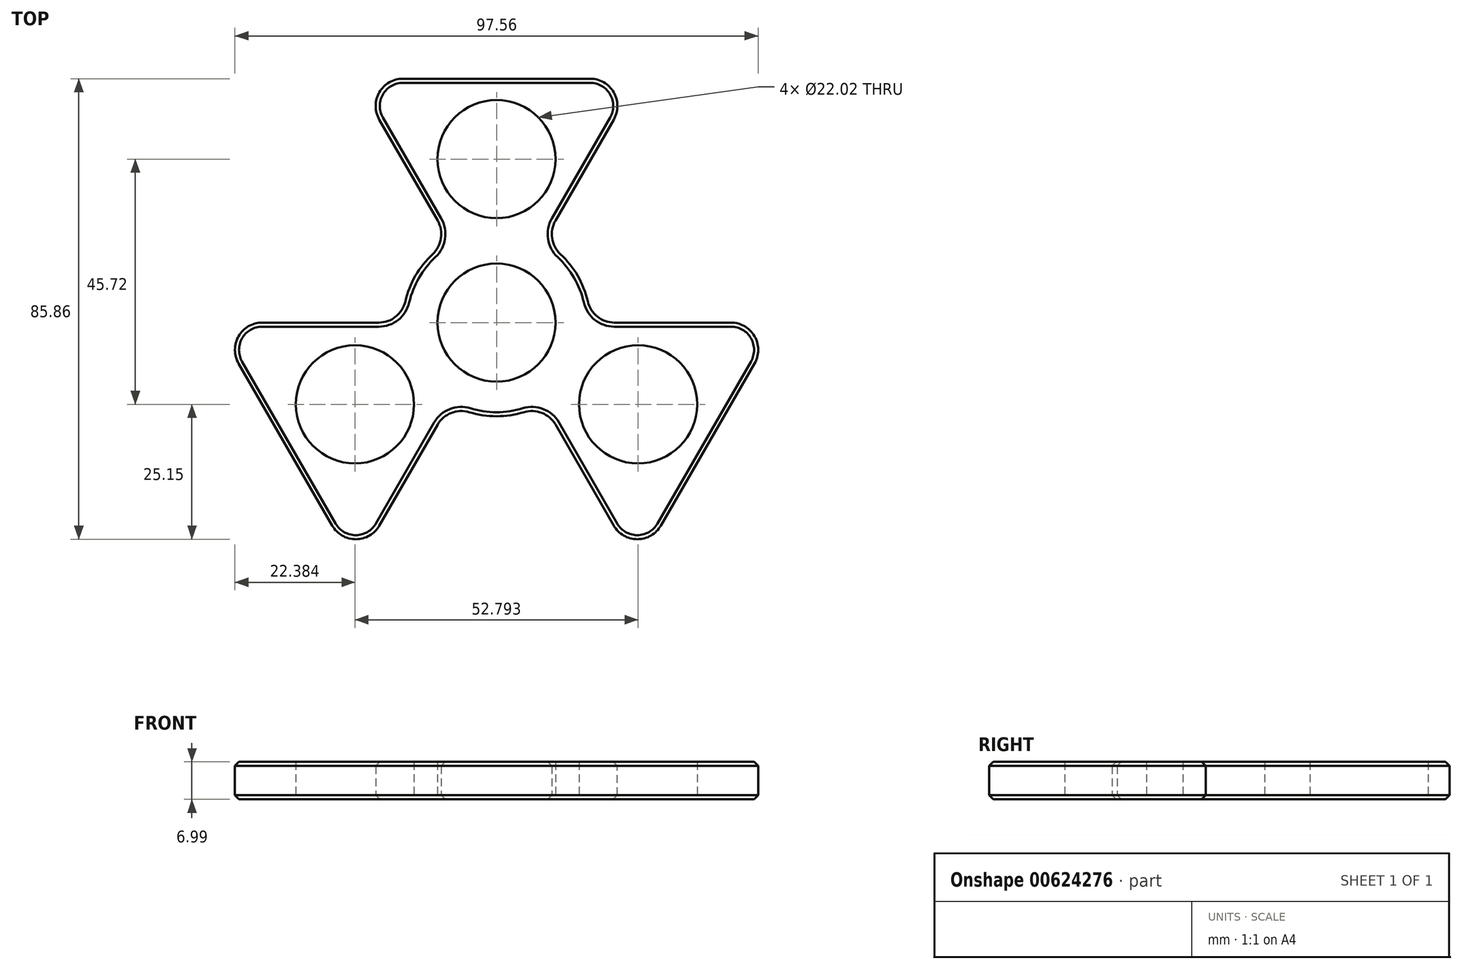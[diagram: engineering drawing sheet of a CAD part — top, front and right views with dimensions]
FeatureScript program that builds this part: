
annotation { "Feature Type Name" : "Feature", "Feature Type Description" : "" }
export const myFeature = defineFeature(function(context is Context, id is Id, definition is map)
    precondition{}
    {
        {
            var Q0;
            Q0=qCreatedBy(makeId("Top.planeOp"),FACE);
            var sketch = newSketch(context, id + "F0", { "sketchPlane" : qUnion([Q0])});
            skCircle(sketch, "E0", {"center": v(0, 0) * mm, "radius": 11.01 * mm});
            skLineSegment(sketch, "E1", {"start": v(0, 0) * mm, "end": v(-26.4, -15.24) * mm});
            skLineSegment(sketch, "E2", {"start": v(-26.4, -15.24) * mm, "end": v(0, 0) * mm});
            skLineSegment(sketch, "E3", {"start": v(0, 0) * mm, "end": v(26.4, -15.24) * mm});
            skLineSegment(sketch, "E4", {"start": v(26.4, -15.24) * mm, "end": v(0, 0) * mm});
            skLineSegment(sketch, "E5", {"start": v(0, 0) * mm, "end": v(0, 30.48) * mm});
            skCircle(sketch, "E6", {"center": v(-26.4, -15.24) * mm, "radius": 11.01 * mm});
            skCircle(sketch, "E7", {"center": v(26.4, -15.24) * mm, "radius": 11.01 * mm});
            skCircle(sketch, "E8", {"center": v(0, 30.48) * mm, "radius": 11.01 * mm});
            skCircle(sketch, "E9", {"center": v(0, 0) * mm, "radius": 14.82 * mm});
            skLineSegment(sketch, "E10", {"start": v(0, 30.48) * mm, "end": v(0, 45.47) * mm});
            skLineSegment(sketch, "E11", {"start": v(-26.4, -15.24) * mm, "end": v(-39.37, -22.73) * mm});
            skLineSegment(sketch, "E12", {"start": v(26.4, -15.24) * mm, "end": v(39.37, -22.73) * mm});
            skLineSegment(sketch, "E13", {"start": v(-39.37, -22.73) * mm, "end": v(-52.5, 0) * mm});
            skLineSegment(sketch, "E14", {"start": v(-39.37, -22.73) * mm, "end": v(-26.25, -45.47) * mm});
            skLineSegment(sketch, "E15", {"start": v(39.37, -22.73) * mm, "end": v(52.5, 0) * mm});
            skLineSegment(sketch, "E16", {"start": v(39.37, -22.73) * mm, "end": v(26.25, -45.47) * mm});
            skLineSegment(sketch, "E17", {"start": v(0, 45.47) * mm, "end": v(-26.25, 45.47) * mm});
            skLineSegment(sketch, "E18", {"start": v(0, 45.47) * mm, "end": v(26.25, 45.47) * mm});
            skLineSegment(sketch, "E19", {"start": v(-14.82, 0) * mm, "end": v(-52.5, 0) * mm});
            skLineSegment(sketch, "E20", {"start": v(-26.25, -45.47) * mm, "end": v(-7.41, -12.84) * mm});
            skLineSegment(sketch, "E21", {"start": v(26.25, -45.47) * mm, "end": v(7.41, -12.84) * mm});
            skLineSegment(sketch, "E22", {"start": v(14.82, 0) * mm, "end": v(52.5, 0) * mm});
            skLineSegment(sketch, "E23", {"start": v(-26.25, 45.47) * mm, "end": v(-7.41, 12.84) * mm});
            skLineSegment(sketch, "E24", {"start": v(26.25, 45.47) * mm, "end": v(7.41, 12.84) * mm});
            skCircle(sketch, "E25", {"center": v(0, 0) * mm, "radius": 17.46 * mm});
            skSolve(sketch);
        }
        {
            var Q0;
            Q0 = qSketchRegion(id + "F0", true);
            var Q1;
            {var subQ4=sQuery(id+"F0.wireOp",EDGE,"E0");var subQ6=sQuery(id+"F0.wireOp",EDGE,"E2");var subQ7=makeQuery(id+"F0.imprint","INTERSECT",VERTEX,{"derivedFrom":[subQ4,subQ6]});Q1=makeQuery(id+"F0.imprint","IMPRINT",FACE,{"disambiguationData":[TD([[makeQuery(id+"F0.imprint","IMPRINT",EDGE,{"disambiguationData":[TD([[subQ7,1.0]])],"derivedFrom":subQ4}),-1.0]])]});}
            var Q2;
            {var subQ4=sQuery(id+"F0.wireOp",EDGE,"E0");var subQ7=sQuery(id+"F0.wireOp",EDGE,"E5");var subQ8=makeQuery(id+"F0.imprint","INTERSECT",VERTEX,{"derivedFrom":[subQ4,subQ7]});Q2=makeQuery(id+"F0.imprint","IMPRINT",FACE,{"disambiguationData":[TD([[makeQuery(id+"F0.imprint","IMPRINT",EDGE,{"disambiguationData":[TD([[subQ8,1.0]])],"derivedFrom":subQ4}),-1.0]])]});}
            var Q3;
            {var subQ1=sQuery(id+"F0.wireOp",EDGE,"E0");var subQ5=sQuery(id+"F0.wireOp",EDGE,"E2");var subQ6=makeQuery(id+"F0.imprint","INTERSECT",VERTEX,{"derivedFrom":[subQ1,subQ5]});Q3=makeQuery(id+"F0.imprint","IMPRINT",FACE,{"disambiguationData":[TD([[makeQuery(id+"F0.imprint","IMPRINT",EDGE,{"disambiguationData":[TD([[subQ6,-1.0]])],"derivedFrom":subQ1}),-1.0]])]});}
            extrude(context, id + "F1", {"entities" : qUnion([Q0, Q1, Q2, Q3]), "depth" : 7 * mm, "offsetDistance" : 25.4 * mm});
        }
        {
            var Q0;
            Q0=makeQuery(id+"F1.opExtrude","SWEPT_EDGE",EDGE,{"disambiguationData":[OSD([sQuery(id+"F0.wireOp",EDGE,"E19"),sQuery(id+"F0.wireOp",EDGE,"jYicORtb-tOr6-X2Lc-VIRF-J2aUJWwLRQqY")])]});
            var Q1;
            Q1=makeQuery(id+"F1.opExtrude","SWEPT_EDGE",EDGE,{"disambiguationData":[OSD([sQuery(id+"F0.wireOp",EDGE,"E23"),sQuery(id+"F0.wireOp",EDGE,"jYicORtb-tOr6-X2Lc-VIRF-J2aUJWwLRQqY")])]});
            var Q2;
            Q2=makeQuery(id+"F1.opExtrude","SWEPT_EDGE",EDGE,{"disambiguationData":[OSD([sQuery(id+"F0.wireOp",EDGE,"E24"),sQuery(id+"F0.wireOp",EDGE,"jYicORtb-tOr6-X2Lc-VIRF-J2aUJWwLRQqY")])]});
            var Q3;
            Q3=makeQuery(id+"F1.opExtrude","SWEPT_EDGE",EDGE,{"disambiguationData":[OSD([sQuery(id+"F0.wireOp",EDGE,"E22"),sQuery(id+"F0.wireOp",EDGE,"jYicORtb-tOr6-X2Lc-VIRF-J2aUJWwLRQqY")])]});
            var Q4;
            Q4=makeQuery(id+"F1.opExtrude","SWEPT_EDGE",EDGE,{"disambiguationData":[OSD([sQuery(id+"F0.wireOp",EDGE,"E20"),sQuery(id+"F0.wireOp",EDGE,"jYicORtb-tOr6-X2Lc-VIRF-J2aUJWwLRQqY")])]});
            var Q5;
            Q5=makeQuery(id+"F1.opExtrude","SWEPT_EDGE",EDGE,{"disambiguationData":[OSD([sQuery(id+"F0.wireOp",EDGE,"E21"),sQuery(id+"F0.wireOp",EDGE,"jYicORtb-tOr6-X2Lc-VIRF-J2aUJWwLRQqY")])]});
            fillet(context, id + "F2", {"entities" : qUnion([Q0, Q1, Q2, Q3, Q4, Q5]), "radius" : 5.08 * mm, "tangentPropagation" : true, "allowEdgeOverflow" : false});
        }
        {
            var Q0;
            Q0=makeQuery(id+"F1.opExtrude","CAP_EDGE",EDGE,{"disambiguationData":[OSD([sQuery(id+"F0.wireOp",EDGE,"E19")])],"isStart":false});
            var Q1;
            Q1=makeQuery(id+"F1.opExtrude","CAP_EDGE",EDGE,{"disambiguationData":[OSD([sQuery(id+"F0.wireOp",EDGE,"E23")])],"isStart":false});
            var Q2;
            Q2=makeQuery(id+"F1.opExtrude","CAP_EDGE",EDGE,{"disambiguationData":[OSD([sQuery(id+"F0.wireOp",EDGE,"E22")])],"isStart":false});
            var Q3;
            Q3=makeQuery(id+"F1.opExtrude","CAP_EDGE",EDGE,{"disambiguationData":[OSD([sQuery(id+"F0.wireOp",EDGE,"E24")])],"isStart":false});
            var Q4;
            Q4=makeQuery(id+"F1.opExtrude","CAP_EDGE",EDGE,{"disambiguationData":[OSD([sQuery(id+"F0.wireOp",EDGE,"E17"),sQuery(id+"F0.wireOp",EDGE,"E18")])],"isStart":false});
            var Q5;
            Q5=makeQuery(id+"F1.opExtrude","CAP_EDGE",EDGE,{"disambiguationData":[OSD([sQuery(id+"F0.wireOp",EDGE,"E13"),sQuery(id+"F0.wireOp",EDGE,"E14")])],"isStart":false});
            var Q6;
            Q6=makeQuery(id+"F1.opExtrude","CAP_EDGE",EDGE,{"disambiguationData":[OSD([sQuery(id+"F0.wireOp",EDGE,"E15"),sQuery(id+"F0.wireOp",EDGE,"E16")])],"isStart":false});
            var Q7;
            Q7=makeQuery(id+"F1.opExtrude","CAP_EDGE",EDGE,{"disambiguationData":[OSD([sQuery(id+"F0.wireOp",EDGE,"E21")])],"isStart":false});
            var Q8;
            Q8=makeQuery(id+"F1.opExtrude","CAP_EDGE",EDGE,{"disambiguationData":[OSD([sQuery(id+"F0.wireOp",EDGE,"E20")])],"isStart":false});
            var Q9;
            Q9=makeQuery(id+"F1.opExtrude","CAP_EDGE",EDGE,{"disambiguationData":[OSD([sQuery(id+"F0.wireOp",EDGE,"E20")])],"isStart":true});
            var Q10;
            Q10=makeQuery(id+"F1.opExtrude","CAP_EDGE",EDGE,{"disambiguationData":[OSD([sQuery(id+"F0.wireOp",EDGE,"E19")])],"isStart":true});
            var Q11;
            Q11=makeQuery(id+"F1.opExtrude","CAP_EDGE",EDGE,{"disambiguationData":[OSD([sQuery(id+"F0.wireOp",EDGE,"E23")])],"isStart":true});
            var Q12;
            Q12=makeQuery(id+"F1.opExtrude","CAP_EDGE",EDGE,{"disambiguationData":[OSD([sQuery(id+"F0.wireOp",EDGE,"E24")])],"isStart":true});
            var Q13;
            Q13=makeQuery(id+"F1.opExtrude","CAP_EDGE",EDGE,{"disambiguationData":[OSD([sQuery(id+"F0.wireOp",EDGE,"E22")])],"isStart":true});
            var Q14;
            Q14=makeQuery(id+"F1.opExtrude","CAP_EDGE",EDGE,{"disambiguationData":[OSD([sQuery(id+"F0.wireOp",EDGE,"E21")])],"isStart":true});
            var Q15;
            Q15=makeQuery(id+"F1.opExtrude","CAP_EDGE",EDGE,{"disambiguationData":[OSD([sQuery(id+"F0.wireOp",EDGE,"E15"),sQuery(id+"F0.wireOp",EDGE,"E16")])],"isStart":true});
            var Q16;
            Q16=makeQuery(id+"F1.opExtrude","CAP_EDGE",EDGE,{"disambiguationData":[OSD([sQuery(id+"F0.wireOp",EDGE,"E17"),sQuery(id+"F0.wireOp",EDGE,"E18")])],"isStart":true});
            var Q17;
            Q17=makeQuery(id+"F1.opExtrude","CAP_EDGE",EDGE,{"disambiguationData":[OSD([sQuery(id+"F0.wireOp",EDGE,"E13"),sQuery(id+"F0.wireOp",EDGE,"E14")])],"isStart":true});
            var Q18;
            {var subQ0=sQuery(id+"F0.wireOp",EDGE,"E9");Q18=makeQuery(id+"F1.opExtrude","CAP_EDGE",EDGE,{"disambiguationData":[OSD([subQ0]),TDD([makeQuery(id+"F0.imprint","IMPRINT",EDGE,{"disambiguationData":[TD([[makeQuery(id+"F0.imprint","INTERSECT",VERTEX,{"derivedFrom":[subQ0,sQuery(id+"F0.wireOp",EDGE,"E19")]}),1.0]])],"derivedFrom":subQ0})])],"isStart":true});}
            var Q19;
            {var subQ0=sQuery(id+"F0.wireOp",EDGE,"E9");Q19=makeQuery(id+"F1.opExtrude","CAP_EDGE",EDGE,{"disambiguationData":[OSD([subQ0]),TDD([makeQuery(id+"F0.imprint","IMPRINT",EDGE,{"disambiguationData":[TD([[makeQuery(id+"F0.imprint","INTERSECT",VERTEX,{"derivedFrom":[subQ0,sQuery(id+"F0.wireOp",EDGE,"E22")]}),-1.0]])],"derivedFrom":subQ0})])],"isStart":true});}
            var Q20;
            {var subQ0=sQuery(id+"F0.wireOp",EDGE,"E9");Q20=makeQuery(id+"F1.opExtrude","CAP_EDGE",EDGE,{"disambiguationData":[OSD([subQ0]),TDD([makeQuery(id+"F0.imprint","IMPRINT",EDGE,{"disambiguationData":[TD([[makeQuery(id+"F0.imprint","INTERSECT",VERTEX,{"derivedFrom":[subQ0,sQuery(id+"F0.wireOp",EDGE,"E20")]}),-1.0]])],"derivedFrom":subQ0})])],"isStart":true});}
            var Q21;
            {var subQ0=sQuery(id+"F0.wireOp",EDGE,"E9");Q21=makeQuery(id+"F1.opExtrude","CAP_EDGE",EDGE,{"disambiguationData":[OSD([subQ0]),TDD([makeQuery(id+"F0.imprint","IMPRINT",EDGE,{"disambiguationData":[TD([[makeQuery(id+"F0.imprint","INTERSECT",VERTEX,{"derivedFrom":[subQ0,sQuery(id+"F0.wireOp",EDGE,"E20")]}),-1.0]])],"derivedFrom":subQ0})])],"isStart":false});}
            var Q22;
            {var subQ0=sQuery(id+"F0.wireOp",EDGE,"E9");Q22=makeQuery(id+"F1.opExtrude","CAP_EDGE",EDGE,{"disambiguationData":[OSD([subQ0]),TDD([makeQuery(id+"F0.imprint","IMPRINT",EDGE,{"disambiguationData":[TD([[makeQuery(id+"F0.imprint","INTERSECT",VERTEX,{"derivedFrom":[subQ0,sQuery(id+"F0.wireOp",EDGE,"E19")]}),1.0]])],"derivedFrom":subQ0})])],"isStart":false});}
            var Q23;
            {var subQ0=sQuery(id+"F0.wireOp",EDGE,"E9");Q23=makeQuery(id+"F1.opExtrude","CAP_EDGE",EDGE,{"disambiguationData":[OSD([subQ0]),TDD([makeQuery(id+"F0.imprint","IMPRINT",EDGE,{"disambiguationData":[TD([[makeQuery(id+"F0.imprint","INTERSECT",VERTEX,{"derivedFrom":[subQ0,sQuery(id+"F0.wireOp",EDGE,"E22")]}),-1.0]])],"derivedFrom":subQ0})])],"isStart":false});}
            chamfer(context, id + "F3", {"entities" : qUnion([Q0, Q1, Q2, Q3, Q4, Q5, Q6, Q7, Q8, Q9, Q10, Q11, Q12, Q13, Q14, Q15, Q16, Q17, Q18, Q19, Q20, Q21, Q22, Q23]), "width" : 0.76 * mm, "tangentPropagation" : true});
        }
    });
